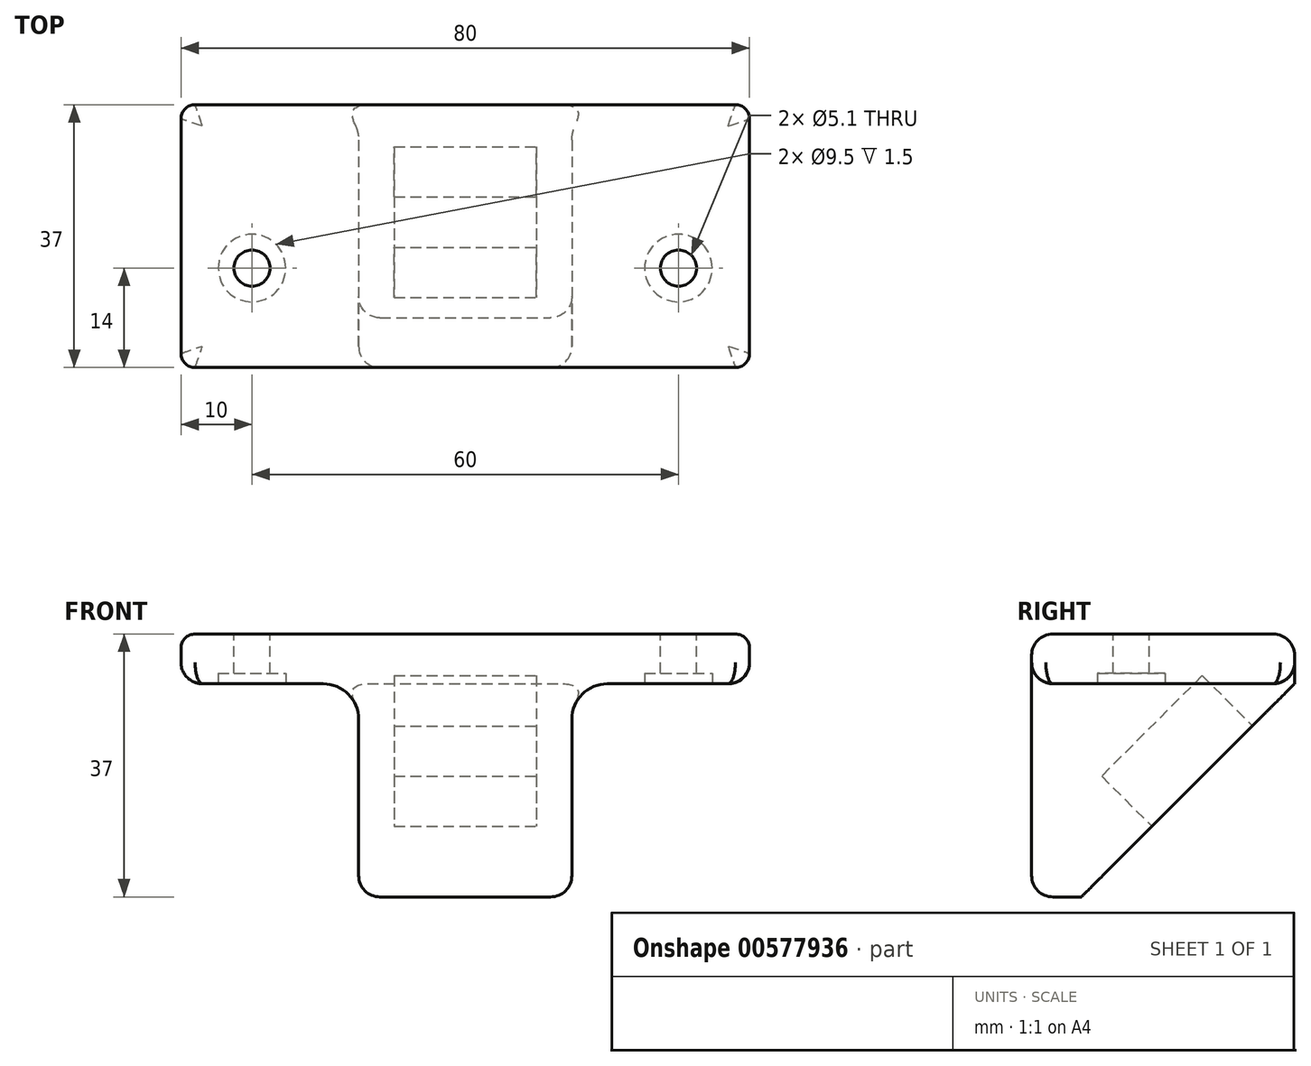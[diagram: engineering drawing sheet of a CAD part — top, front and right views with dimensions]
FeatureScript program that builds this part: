
annotation { "Feature Type Name" : "Feature", "Feature Type Description" : "" }
export const myFeature = defineFeature(function(context is Context, id is Id, definition is map)
    precondition{}
    {
        {
            var Q0;
            Q0=qCreatedBy(makeId("Right.planeOp"),FACE);
            var sketch = newSketch(context, id + "F0", { "sketchPlane" : qUnion([Q0])});
            skLineSegment(sketch, "E0.top", {"start": v(20, 20) * mm, "end": v(-20, 20) * mm});
            skLineSegment(sketch, "E0.right", {"start": v(-20, -20) * mm, "end": v(-20, 20) * mm});
            skPoint(sketch, "E0.middle", {"position": v(0, 0) * mm});
            skLineSegment(sketch, "E1", {"start": v(20, 20) * mm, "end": v(-20, -20) * mm});
            skSolve(sketch);
        }
        {
            var Q0;
            Q0 = qSketchRegion(id + "F0", true);
            extrude(context, id + "F1", {"entities" : qUnion([Q0]), "depth" : 80 * mm, "offsetDistance" : 25 * mm});
        }
        {
            var Q0;
            Q0=makeQuery(id+"F1.opExtrude","SWEPT_FACE",FACE,{"disambiguationData":[OSD([sQuery(id+"F0.wireOp",EDGE,"E1")])]});
            var sketch = newSketch(context, id + "F2", { "sketchPlane" : qUnion([Q0])});
            skLineSegment(sketch, "E2", {"start": v(-40, 28.28) * mm, "end": v(-40, -28.28) * mm, "construction": true});
            skLineSegment(sketch, "E3", {"start": v(-80, 0) * mm, "end": v(0, 0) * mm, "construction": true});
            skLineSegment(sketch, "E4.bottom", {"start": v(-30, 10) * mm, "end": v(-50, 10) * mm});
            skLineSegment(sketch, "E4.top", {"start": v(-30, -10) * mm, "end": v(-50, -10) * mm});
            skLineSegment(sketch, "E4.left", {"start": v(-30, 10) * mm, "end": v(-30, -10) * mm});
            skLineSegment(sketch, "E4.right", {"start": v(-50, 10) * mm, "end": v(-50, -10) * mm});
            skPoint(sketch, "E4.middle", {"position": v(-40, 0) * mm});
            skSolve(sketch);
        }
        {
            var Q0;
            Q0 = qSketchRegion(id + "F2", true);
            extrude(context, id + "F3", {"entities" : qUnion([Q0]), "operationType" : NewBodyOperationType.REMOVE, "oppositeDirection" : true, "depth" : 10 * mm, "offsetDistance" : 25 * mm});
        }
        {
            var Q0;
            Q0=makeQuery(id+"F1.opExtrude","CAP_FACE",FACE,{"disambiguationData":[OSD([sQuery(id+"F0.wireOp",EDGE,"E0.top"),sQuery(id+"F0.wireOp",EDGE,"E0.right"),sQuery(id+"F0.wireOp",EDGE,"E1")])],"isStart":false});
            var sketch = newSketch(context, id + "F4", { "sketchPlane" : qUnion([Q0])});
            skLineSegment(sketch, "E5.0", {"start": v(-17, -17) * mm, "end": v(-17, 13) * mm});
            skLineSegment(sketch, "E5.1", {"start": v(13, 13) * mm, "end": v(-17, 13) * mm});
            skLineSegment(sketch, "E6", {"start": v(-17, -17) * mm, "end": v(13, 13) * mm});
            skLineSegment(sketch, "E7.trimOffspring", {"start": v(13, 13) * mm, "end": v(-17, -17) * mm, "construction": true});
            skPoint(sketch, "E8.0.start.orphan", {"position": v(20, 20) * mm});
            skPoint(sketch, "E9.orphan", {"position": v(-20, -20) * mm});
            skSolve(sketch);
        }
        {
            var Q0;
            Q0=makeQuery(id+"F4.imprint","IMPRINT",FACE,{"disambiguationData":[TD([[makeQuery(id+"F4.imprint","IMPRINT",EDGE,{"derivedFrom":sQuery(id+"F4.wireOp",EDGE,"E5.0")}),-1.0]])]});
            extrude(context, id + "F5", {"entities" : qUnion([Q0]), "operationType" : NewBodyOperationType.REMOVE, "oppositeDirection" : true, "depth" : 25 * mm, "offsetDistance" : 25 * mm});
        }
        {
            var Q0;
            Q0=makeQuery(id+"F1.opExtrude","CAP_FACE",FACE,{"disambiguationData":[OSD([sQuery(id+"F0.wireOp",EDGE,"E0.top"),sQuery(id+"F0.wireOp",EDGE,"E0.right"),sQuery(id+"F0.wireOp",EDGE,"E1")])],"isStart":false});
            var sketch = newSketch(context, id + "F6", { "sketchPlane" : qUnion([Q0])});
            skLineSegment(sketch, "E10", {"start": v(-20, 20) * mm, "end": v(-24, 20) * mm});
            skLineSegment(sketch, "E11", {"start": v(-24, 20) * mm, "end": v(-24, -24) * mm});
            skPoint(sketch, "E12.0", {"position": v(-20, -20) * mm});
            skLineSegment(sketch, "E13", {"start": v(-20, -20) * mm, "end": v(-24, -24) * mm});
            skLineSegment(sketch, "E14.0", {"start": v(-20, -17.17) * mm, "end": v(-20, 20) * mm});
            skLineSegment(sketch, "E15.0", {"start": v(-20, -20) * mm, "end": v(-20, -17.17) * mm});
            skLineSegment(sketch, "E16.0.0", {"start": v(-20, -17.17) * mm, "end": v(-20, -20) * mm});
            skLineSegment(sketch, "E16.0.1", {"start": v(-20, -20) * mm, "end": v(-17.59, -17.59) * mm});
            skPoint(sketch, "E16.0.3.end.orphan", {"position": v(-19, -16.17) * mm});
            skSolve(sketch);
        }
        {
            var Q0;
            Q0 = qSketchRegion(id + "F6", true);
            var Q1;
            Q1=makeQuery(id+"F1.opExtrude","CAP_FACE",FACE,{"disambiguationData":[OSD([sQuery(id+"F0.wireOp",EDGE,"E0.top"),sQuery(id+"F0.wireOp",EDGE,"E0.right"),sQuery(id+"F0.wireOp",EDGE,"E1")])],"isStart":true});
            extrude(context, id + "F7", {"entities" : qUnion([Q0]), "operationType" : NewBodyOperationType.ADD, "endBound" : BoundingType.UP_TO_SURFACE, "oppositeDirection" : true, "depth" : 78 * mm, "endBoundEntityFace" : qUnion([Q1]), "offsetDistance" : 25 * mm});
        }
        {
            var Q0;
            Q0=makeQuery(id+"F1.opExtrude","CAP_FACE",FACE,{"disambiguationData":[OSD([sQuery(id+"F0.wireOp",EDGE,"E0.top"),sQuery(id+"F0.wireOp",EDGE,"E0.right"),sQuery(id+"F0.wireOp",EDGE,"E1")])],"isStart":true});
            var sketch = newSketch(context, id + "F8", { "sketchPlane" : qUnion([Q0])});
            skLineSegment(sketch, "E17.0", {"start": v(-13, 13) * mm, "end": v(17, 13) * mm});
            skLineSegment(sketch, "E18.0", {"start": v(17, -17) * mm, "end": v(17, 13) * mm});
            skLineSegment(sketch, "E19.0", {"start": v(-13, 13) * mm, "end": v(17, -17) * mm});
            skSolve(sketch);
        }
        {
            var Q0;
            Q0 = qSketchRegion(id + "F8", true);
            extrude(context, id + "F9", {"entities" : qUnion([Q0]), "operationType" : NewBodyOperationType.REMOVE, "oppositeDirection" : true, "depth" : 25 * mm, "offsetDistance" : 25 * mm});
        }
        {
            var Q0;
            Q0=makeQuery(id+"F1.opExtrude","SWEPT_FACE",FACE,{"disambiguationData":[OSD([sQuery(id+"F0.wireOp",EDGE,"E0.top")])]});
            var sketch = newSketch(context, id + "F10", { "sketchPlane" : qUnion([Q0])});
            skLineSegment(sketch, "E20.0", {"start": v(55, 13) * mm, "end": v(55, -17) * mm, "construction": true});
            skLineSegment(sketch, "E21.0", {"start": v(55, 13) * mm, "end": v(80, 13) * mm, "construction": true});
            skLineSegment(sketch, "E22.0", {"start": v(25, 13) * mm, "end": v(25, -17) * mm, "construction": true});
            skLineSegment(sketch, "E23.0", {"start": v(25, 13) * mm, "end": v(0, 13) * mm, "construction": true});
            skLineSegment(sketch, "E24.0", {"start": v(55, -17) * mm, "end": v(80, -17) * mm, "construction": true});
            skCircle(sketch, "E25", {"center": v(10, -10) * mm, "radius": 2.55 * mm});
            skCircle(sketch, "E26", {"center": v(70, -10) * mm, "radius": 2.55 * mm});
            skLineSegment(sketch, "E27", {"start": v(70, -10) * mm, "end": v(80, -10) * mm, "construction": true});
            skLineSegment(sketch, "E28", {"start": v(10, -10) * mm, "end": v(0, -10) * mm, "construction": true});
            skSolve(sketch);
        }
        {
            var Q0;
            Q0 = qSketchRegion(id + "F10", true);
            extrude(context, id + "F11", {"entities" : qUnion([Q0]), "operationType" : NewBodyOperationType.REMOVE, "endBound" : BoundingType.THROUGH_ALL, "oppositeDirection" : true, "depth" : 25 * mm, "offsetDistance" : 25 * mm});
        }
        {
            var Q0;
            Q0=makeQuery(id+"F9.boolean.opBoolean","COPY",FACE,{"derivedFrom":makeQuery(id+"F9.opExtrude","SWEPT_FACE",FACE,{"disambiguationData":[OSD([sQuery(id+"F8.wireOp",EDGE,"E17.0")])]})});
            var sketch = newSketch(context, id + "F12", { "sketchPlane" : qUnion([Q0])});
            skCircle(sketch, "E29.0", {"center": v(10, 10) * mm, "radius": 2.55 * mm, "construction": true});
            skCircle(sketch, "E30.0", {"center": v(70, 10) * mm, "radius": 2.55 * mm, "construction": true});
            skCircle(sketch, "E31", {"center": v(10, 10) * mm, "radius": 4.75 * mm});
            skCircle(sketch, "E32", {"center": v(70, 10) * mm, "radius": 4.75 * mm});
            skSolve(sketch);
        }
        {
            var Q0;
            Q0 = qSketchRegion(id + "F12", true);
            extrude(context, id + "F13", {"entities" : qUnion([Q0]), "operationType" : NewBodyOperationType.REMOVE, "oppositeDirection" : true, "depth" : 1.5 * mm, "offsetDistance" : 25 * mm});
        }
        {
            var Q0;
            Q0=makeQuery(id+"F5.boolean.opBoolean","COPY",FACE,{"derivedFrom":makeQuery(id+"F5.opExtrude","SWEPT_FACE",FACE,{"disambiguationData":[OSD([sQuery(id+"F4.wireOp",EDGE,"E5.0")])]})});
            var sketch = newSketch(context, id + "F14", { "sketchPlane" : qUnion([Q0])});
            skLineSegment(sketch, "E33.0", {"start": v(-55, 13) * mm, "end": v(-55, -17) * mm, "construction": true});
            skLineSegment(sketch, "E34.0", {"start": v(-55, 13) * mm, "end": v(-80, 13) * mm, "construction": true});
            skLineSegment(sketch, "E35.0", {"start": v(-25, 13) * mm, "end": v(0, 13) * mm, "construction": true});
            skLineSegment(sketch, "E36.0", {"start": v(-25, 13) * mm, "end": v(-25, -17) * mm, "construction": true});
            skLineSegment(sketch, "E37.0", {"start": v(-25, -17) * mm, "end": v(0, -17) * mm, "construction": true});
            skPoint(sketch, "E38.0", {"position": v(-67.5, -17) * mm});
            skLineSegment(sketch, "E39.0", {"start": v(-55, -17) * mm, "end": v(-80, -17) * mm, "construction": true});
            skLineSegment(sketch, "E40", {"start": v(-67.5, 13) * mm, "end": v(-67.5, -17) * mm, "construction": true});
            skLineSegment(sketch, "E41", {"start": v(-12.5, 13) * mm, "end": v(-12.5, -17) * mm, "construction": true});
            skCircle(sketch, "E42", {"center": v(-70, 0) * mm, "radius": 1.93 * mm});
            skCircle(sketch, "E43", {"center": v(-10, 0) * mm, "radius": 1.93 * mm});
            skLineSegment(sketch, "E44", {"start": v(-12.5, -2) * mm, "end": v(-10, 0) * mm, "construction": true});
            skLineSegment(sketch, "E45", {"start": v(-67.5, -2) * mm, "end": v(-70, 0) * mm, "construction": true});
            skSolve(sketch);
        }
        {
            var Q0;
            Q0 = qSketchRegion(id + "F14", true);
            extrude(context, id + "F15", {"entities" : qUnion([Q0]), "operationType" : NewBodyOperationType.REMOVE, "endBound" : BoundingType.THROUGH_ALL, "oppositeDirection" : true, "depth" : 25 * mm, "offsetDistance" : 25 * mm});
        }
        {
            var Q0;
            Q0=makeQuery(id+"F5.boolean.opBoolean","COPY",FACE,{"derivedFrom":makeQuery(id+"F5.opExtrude","SWEPT_FACE",FACE,{"disambiguationData":[OSD([sQuery(id+"F4.wireOp",EDGE,"E5.0")])]})});
            var sketch = newSketch(context, id + "F16", { "sketchPlane" : qUnion([Q0])});
            skCircle(sketch, "E46.0", {"center": v(-10, 0) * mm, "radius": 1.93 * mm, "construction": true});
            skCircle(sketch, "E47.0", {"center": v(-70, 0) * mm, "radius": 1.93 * mm, "construction": true});
            skCircle(sketch, "E48", {"center": v(-70, 0) * mm, "radius": 4.55 * mm});
            skCircle(sketch, "E49", {"center": v(-10, 0) * mm, "radius": 4.55 * mm});
            skSolve(sketch);
        }
        {
            var Q0;
            Q0 = qSketchRegion(id + "F16", true);
            extrude(context, id + "F17", {"entities" : qUnion([Q0]), "operationType" : NewBodyOperationType.REMOVE, "oppositeDirection" : true, "depth" : 1.5 * mm, "offsetDistance" : 25 * mm});
        }
        {
            var Q0;
            Q0=makeQuery(id+"F7.boolean.opBoolean","MERGE",FACE,{"derivedFrom":[makeQuery(id+"F1.opExtrude","CAP_FACE",FACE,{"disambiguationData":[OSD([sQuery(id+"F0.wireOp",EDGE,"E0.top"),sQuery(id+"F0.wireOp",EDGE,"E0.right"),sQuery(id+"F0.wireOp",EDGE,"E1")])],"isStart":false}),makeQuery(id+"F7.opExtrude","CAP_FACE",FACE,{"disambiguationData":[OSD([sQuery(id+"F6.wireOp",EDGE,"E10"),sQuery(id+"F6.wireOp",EDGE,"E11"),sQuery(id+"F6.wireOp",EDGE,"E13"),sQuery(id+"F6.wireOp",EDGE,"E14.0"),sQuery(id+"F6.wireOp",EDGE,"E16.0.0")])],"isStart":true})]});
            var sketch = newSketch(context, id + "F18", { "sketchPlane" : qUnion([Q0])});
            skLineSegment(sketch, "E50", {"start": v(13, 13) * mm, "end": v(13, 24.34) * mm});
            skLineSegment(sketch, "E51", {"start": v(13, 24.34) * mm, "end": v(28.5, 24.34) * mm});
            skLineSegment(sketch, "E52", {"start": v(28.5, 24.34) * mm, "end": v(24, -31.51) * mm});
            skLineSegment(sketch, "E53", {"start": v(24, -31.51) * mm, "end": v(-23.57, -31.51) * mm});
            skLineSegment(sketch, "E54", {"start": v(-17, -17) * mm, "end": v(-30.86, -17) * mm});
            skLineSegment(sketch, "E55", {"start": v(-30.86, -17) * mm, "end": v(-23.57, -31.51) * mm});
            skLineSegment(sketch, "E56", {"start": v(13, 13) * mm, "end": v(-17, -17) * mm});
            skSolve(sketch);
        }
        {
            var Q0;
            Q0 = qSketchRegion(id + "F18", true);
            extrude(context, id + "F19", {"entities" : qUnion([Q0]), "operationType" : NewBodyOperationType.REMOVE, "oppositeDirection" : true, "depth" : 85.2 * mm, "offsetDistance" : 25 * mm});
        }
        {
            var Q0;
            Q0=makeQuery(id+"F5.boolean.opBoolean","COPY",FACE,{"derivedFrom":makeQuery(id+"F5.opExtrude","SWEPT_FACE",FACE,{"disambiguationData":[OSD([sQuery(id+"F4.wireOp",EDGE,"E5.0")])]})});
            var sketch = newSketch(context, id + "F20", { "sketchPlane" : qUnion([Q0])});
            skLineSegment(sketch, "E57.0.0", {"start": v(-80, 13) * mm, "end": v(-80, -17) * mm, "construction": true});
            skLineSegment(sketch, "E57.0.1", {"start": v(-80, -17) * mm, "end": v(-55, -17) * mm, "construction": true});
            skLineSegment(sketch, "E57.0.2", {"start": v(-55, -17) * mm, "end": v(-55, 13) * mm, "construction": true});
            skLineSegment(sketch, "E57.0.3", {"start": v(-55, 13) * mm, "end": v(-80, 13) * mm, "construction": true});
            skLineSegment(sketch, "E58.0", {"start": v(-25, 13) * mm, "end": v(0, 13) * mm, "construction": true});
            skLineSegment(sketch, "E59.bottom", {"start": v(-80, 13) * mm, "end": v(-55, 13) * mm});
            skLineSegment(sketch, "E59.top", {"start": v(-80, -17) * mm, "end": v(-55, -17) * mm});
            skLineSegment(sketch, "E59.left", {"start": v(-80, 13) * mm, "end": v(-80, -17) * mm});
            skLineSegment(sketch, "E59.right", {"start": v(-55, 13) * mm, "end": v(-55, -17) * mm});
            skLineSegment(sketch, "E60.0", {"start": v(-25, -17) * mm, "end": v(0, -17) * mm, "construction": true});
            skLineSegment(sketch, "E61.bottom", {"start": v(-25, 13) * mm, "end": v(0, 13) * mm});
            skLineSegment(sketch, "E61.top", {"start": v(-25, -17) * mm, "end": v(0, -17) * mm});
            skLineSegment(sketch, "E61.left", {"start": v(-25, 13) * mm, "end": v(-25, -17) * mm});
            skLineSegment(sketch, "E61.right", {"start": v(0, 13) * mm, "end": v(0, -17) * mm});
            skSolve(sketch);
        }
        {
            var Q0;
            Q0 = qSketchRegion(id + "F20", true);
            extrude(context, id + "F21", {"entities" : qUnion([Q0]), "operationType" : NewBodyOperationType.REMOVE, "oppositeDirection" : true, "depth" : 25 * mm, "offsetDistance" : 25 * mm});
        }
        {
            var Q0;
            Q0=makeQuery(id+"F9.boolean.opBoolean","COPY",EDGE,{"derivedFrom":makeQuery(id+"F9.opExtrude","SWEPT_EDGE",EDGE,{"disambiguationData":[OSD([sQuery(id+"F8.wireOp",EDGE,"E17.0"),sQuery(id+"F8.wireOp",EDGE,"E18.0")])]})});
            var Q1;
            Q1=makeQuery(id+"F5.boolean.opBoolean","COPY",EDGE,{"derivedFrom":makeQuery(id+"F5.opExtrude","SWEPT_EDGE",EDGE,{"disambiguationData":[OSD([sQuery(id+"F4.wireOp",EDGE,"E5.0"),sQuery(id+"F4.wireOp",EDGE,"E5.1")])]})});
            var Q2;
            Q2=makeQuery(id+"F7.opExtrude","SWEPT_EDGE",EDGE,{"disambiguationData":[OSD([sQuery(id+"F6.wireOp",EDGE,"E10"),sQuery(id+"F6.wireOp",EDGE,"E11")])]});
            var Q3;
            Q3=makeQuery(id+"F19.boolean.opBoolean","INTERSECT",EDGE,{"derivedFrom":[makeQuery(id+"F7.boolean.opBoolean","MERGE",FACE,{"derivedFrom":[makeQuery(id+"F1.opExtrude","SWEPT_FACE",FACE,{"disambiguationData":[OSD([sQuery(id+"F0.wireOp",EDGE,"E0.top")])]}),makeQuery(id+"F7.opExtrude","SWEPT_FACE",FACE,{"disambiguationData":[OSD([sQuery(id+"F6.wireOp",EDGE,"E10")])]})]}),makeQuery(id+"F19.opExtrude","SWEPT_FACE",FACE,{"disambiguationData":[OSD([sQuery(id+"F18.wireOp",EDGE,"E50")])]})]});
            var Q4;
            Q4=makeQuery(id+"F19.boolean.opBoolean","INTERSECT",EDGE,{"derivedFrom":[makeQuery(id+"F7.opExtrude","SWEPT_FACE",FACE,{"disambiguationData":[OSD([sQuery(id+"F6.wireOp",EDGE,"E11")])]}),makeQuery(id+"F19.opExtrude","SWEPT_FACE",FACE,{"disambiguationData":[OSD([sQuery(id+"F18.wireOp",EDGE,"E54")])]})]});
            var Q5;
            {var subQ0=sQuery(id+"F6.wireOp",EDGE,"E13");var subQ1=sQuery(id+"F0.wireOp",EDGE,"E1");Q5=makeQuery(id+"F19.boolean.opBoolean","MERGE",EDGE,{"derivedFrom":[makeQuery(id+"F9.boolean.opBoolean","COPY",EDGE,{"derivedFrom":makeQuery(id+"F9.opExtrude","SWEPT_EDGE",EDGE,{"disambiguationData":[OSD([sQuery(id+"F0.wireOp",EDGE,"E0.top"),sQuery(id+"F0.wireOp",EDGE,"E0.right"),subQ1,subQ0,sQuery(id+"F8.wireOp",EDGE,"E18.0"),sQuery(id+"F8.wireOp",EDGE,"E19.0")])]})}),makeQuery(id+"F19.opExtrude","SWEPT_EDGE",EDGE,{"disambiguationData":[OSD([subQ1,sQuery(id+"F4.wireOp",EDGE,"E5.0"),subQ0,sQuery(id+"F18.wireOp",EDGE,"E54"),sQuery(id+"F18.wireOp",EDGE,"E56")])]})]});}
            var Q6;
            {var subQ0=sQuery(id+"F4.wireOp",EDGE,"E5.0");var subQ1=sQuery(id+"F0.wireOp",EDGE,"E1");Q6=makeQuery(id+"F19.boolean.opBoolean","MERGE",EDGE,{"derivedFrom":[makeQuery(id+"F5.boolean.opBoolean","COPY",EDGE,{"derivedFrom":makeQuery(id+"F5.opExtrude","SWEPT_EDGE",EDGE,{"disambiguationData":[OSD([subQ1,subQ0,sQuery(id+"F4.wireOp",EDGE,"E6")])]})}),makeQuery(id+"F19.opExtrude","SWEPT_EDGE",EDGE,{"disambiguationData":[OSD([subQ1,subQ0,sQuery(id+"F6.wireOp",EDGE,"E13"),sQuery(id+"F18.wireOp",EDGE,"E54"),sQuery(id+"F18.wireOp",EDGE,"E56")])]})]});}
            var Q7;
            {var subQ0=sQuery(id+"F4.wireOp",EDGE,"E5.1");var subQ1=sQuery(id+"F0.wireOp",EDGE,"E1");Q7=makeQuery(id+"F19.boolean.opBoolean","MERGE",EDGE,{"derivedFrom":[makeQuery(id+"F5.boolean.opBoolean","COPY",EDGE,{"derivedFrom":makeQuery(id+"F5.opExtrude","SWEPT_EDGE",EDGE,{"disambiguationData":[OSD([subQ1,subQ0,sQuery(id+"F4.wireOp",EDGE,"E6")])]})}),makeQuery(id+"F19.opExtrude","SWEPT_EDGE",EDGE,{"disambiguationData":[OSD([subQ1,subQ0,sQuery(id+"F18.wireOp",EDGE,"E50"),sQuery(id+"F18.wireOp",EDGE,"E56")])]})]});}
            var Q8;
            {var subQ0=sQuery(id+"F0.wireOp",EDGE,"E1");Q8=makeQuery(id+"F19.boolean.opBoolean","MERGE",EDGE,{"derivedFrom":[makeQuery(id+"F9.boolean.opBoolean","COPY",EDGE,{"derivedFrom":makeQuery(id+"F9.opExtrude","SWEPT_EDGE",EDGE,{"disambiguationData":[OSD([sQuery(id+"F0.wireOp",EDGE,"E0.top"),sQuery(id+"F0.wireOp",EDGE,"E0.right"),subQ0,sQuery(id+"F6.wireOp",EDGE,"E13"),sQuery(id+"F8.wireOp",EDGE,"E17.0"),sQuery(id+"F8.wireOp",EDGE,"E19.0")])]})}),makeQuery(id+"F19.opExtrude","SWEPT_EDGE",EDGE,{"disambiguationData":[OSD([subQ0,sQuery(id+"F4.wireOp",EDGE,"E5.1"),sQuery(id+"F18.wireOp",EDGE,"E50"),sQuery(id+"F18.wireOp",EDGE,"E56")])]})]});}
            fillet(context, id + "F22", {"entities" : qUnion([Q0, Q1, Q2, Q3, Q4, Q5, Q6, Q7, Q8]), "radius" : 3 * mm, "tangentPropagation" : true, "allowEdgeOverflow" : false});
        }
        {
            var Q0;
            {var subQ0=sQuery(id+"F0.wireOp",EDGE,"E0.top");Q0=makeQuery(id+"F7.boolean.opBoolean","MERGE",EDGE,{"derivedFrom":[makeQuery(id+"F1.opExtrude","CAP_EDGE",EDGE,{"disambiguationData":[OSD([subQ0])],"isStart":true}),makeQuery(id+"F7.opExtrude","TWEAK_EDGE",EDGE,{"derivedFrom":[makeQuery(id+"F1.opExtrude","CAP_FACE",FACE,{"disambiguationData":[OSD([subQ0,sQuery(id+"F0.wireOp",EDGE,"E0.right"),sQuery(id+"F0.wireOp",EDGE,"E1")])],"isStart":true}),makeQuery(id+"F6.imprint","IMPRINT",EDGE,{"derivedFrom":sQuery(id+"F6.wireOp",EDGE,"E10")})]})]});}
            var Q1;
            Q1=makeQuery(id+"F7.boolean.opBoolean","MERGE",EDGE,{"derivedFrom":[makeQuery(id+"F1.opExtrude","CAP_EDGE",EDGE,{"disambiguationData":[OSD([sQuery(id+"F0.wireOp",EDGE,"E0.top")])],"isStart":false}),makeQuery(id+"F7.opExtrude","CAP_EDGE",EDGE,{"disambiguationData":[OSD([sQuery(id+"F6.wireOp",EDGE,"E10")])],"isStart":true})]});
            fillet(context, id + "F23", {"entities" : qUnion([Q0, Q1]), "radius" : 2 * mm, "tangentPropagation" : true, "allowEdgeOverflow" : false});
        }
        {
            var Q0;
            Q0=makeQuery(id+"F21.boolean.opBoolean","MERGE",EDGE,{"derivedFrom":[makeQuery(id+"F5.boolean.opBoolean","COPY",EDGE,{"derivedFrom":makeQuery(id+"F5.opExtrude","CAP_EDGE",EDGE,{"disambiguationData":[OSD([sQuery(id+"F4.wireOp",EDGE,"E5.1")])],"isStart":false})}),makeQuery(id+"F21.opExtrude","SWEPT_EDGE",EDGE,{"disambiguationData":[OSD([sQuery(id+"F20.wireOp",EDGE,"E59.bottom"),sQuery(id+"F20.wireOp",EDGE,"E59.right")])]})]});
            var Q1;
            Q1=makeQuery(id+"F21.boolean.opBoolean","MERGE",EDGE,{"derivedFrom":[makeQuery(id+"F9.boolean.opBoolean","COPY",EDGE,{"derivedFrom":makeQuery(id+"F9.opExtrude","CAP_EDGE",EDGE,{"disambiguationData":[OSD([sQuery(id+"F8.wireOp",EDGE,"E17.0")])],"isStart":false})}),makeQuery(id+"F21.opExtrude","SWEPT_EDGE",EDGE,{"disambiguationData":[OSD([sQuery(id+"F20.wireOp",EDGE,"E61.bottom"),sQuery(id+"F20.wireOp",EDGE,"E61.left")])]})]});
            fillet(context, id + "F24", {"entities" : qUnion([Q0, Q1]), "radius" : 5 * mm, "tangentPropagation" : true, "allowEdgeOverflow" : false});
        }
        {
            var Q0;
            Q0=makeQuery(id+"F21.boolean.opBoolean","INTERSECT",EDGE,{"derivedFrom":[makeQuery(id+"F7.opExtrude","SWEPT_FACE",FACE,{"disambiguationData":[OSD([sQuery(id+"F6.wireOp",EDGE,"E11")])]}),makeQuery(id+"F21.opExtrude","SWEPT_FACE",FACE,{"disambiguationData":[OSD([sQuery(id+"F20.wireOp",EDGE,"E59.right")])]})]});
            var Q1;
            Q1=makeQuery(id+"F21.boolean.opBoolean","INTERSECT",EDGE,{"derivedFrom":[makeQuery(id+"F7.opExtrude","SWEPT_FACE",FACE,{"disambiguationData":[OSD([sQuery(id+"F6.wireOp",EDGE,"E11")])]}),makeQuery(id+"F21.opExtrude","SWEPT_FACE",FACE,{"disambiguationData":[OSD([sQuery(id+"F20.wireOp",EDGE,"E61.left")])]})]});
            fillet(context, id + "F25", {"entities" : qUnion([Q0, Q1]), "radius" : 3 * mm, "tangentPropagation" : true, "allowEdgeOverflow" : false});
        }
    });
